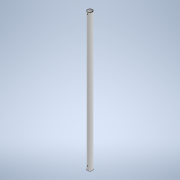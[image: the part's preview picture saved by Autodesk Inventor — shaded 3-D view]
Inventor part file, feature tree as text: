
AUTODESK INVENTOR PART (.ipt)
format: ipt  version: 2022 (Build 260153000, 153)  size: 174,592 bytes
history: native  units: mm
features: extrude x2, sketch x2
ambient origin geometry x8: Origin, YZ Plane, XZ Plane, XY Plane, X Axis, Y Axis, Z Axis, Center Point
bodies: Body1 (feature_tree)
feature tree (4):
  extrude  "Extrusion5"  Depth=18.0mm
  extrude  "Extrusion6"  Depth=10.0mm TaperAngle=0.0deg
  sketch  "Sketch2"  dims[d31=34.456mm d91=18.0mm]
  sketch  "Sketch3"  dims[d92=16.0mm d93=500.0mm d94=0.0mm d95=15.0mm d96=3.0mm d97=6.0mm d98=3.0mm d99=10.0mm d100=10.0mm d101=0.0mm d102=0.0mm]
